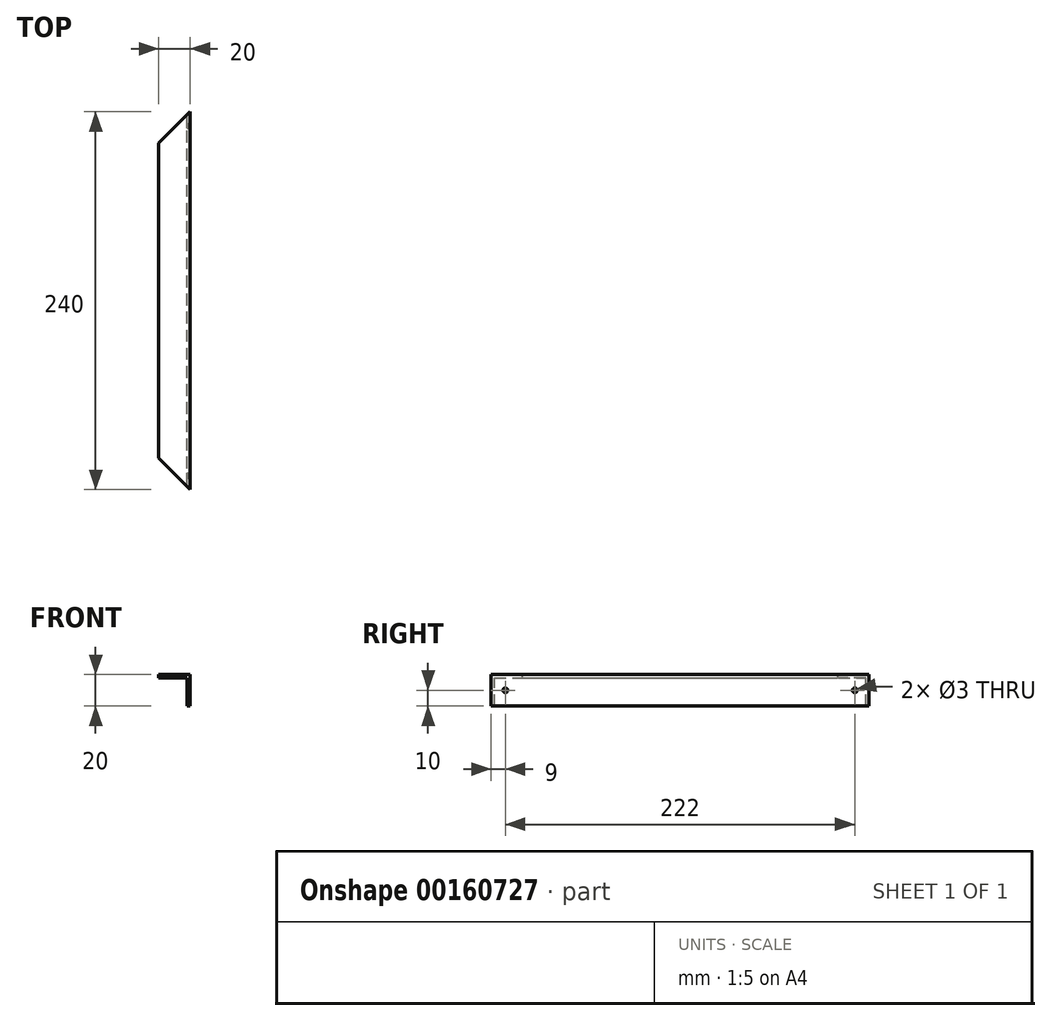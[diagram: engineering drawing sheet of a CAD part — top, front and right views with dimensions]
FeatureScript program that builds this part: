
annotation { "Feature Type Name" : "Feature", "Feature Type Description" : "" }
export const myFeature = defineFeature(function(context is Context, id is Id, definition is map)
    precondition{}
    {
        {
            var Q0;
            Q0=qCreatedBy(makeId("Front.planeOp"),FACE);
            var sketch = newSketch(context, id + "F0", { "sketchPlane" : qUnion([Q0])});
            skLineSegment(sketch, "E0", {"start": v(0, 0) * mm, "end": v(0, 20) * mm});
            skLineSegment(sketch, "E1", {"start": v(0, 20) * mm, "end": v(-20, 20) * mm});
            skLineSegment(sketch, "E2", {"start": v(-20, 20) * mm, "end": v(-20, 18) * mm});
            skLineSegment(sketch, "E3", {"start": v(-20, 18) * mm, "end": v(-2, 18) * mm});
            skLineSegment(sketch, "E4", {"start": v(-2, 18) * mm, "end": v(-2, 0) * mm});
            skLineSegment(sketch, "E5", {"start": v(-2, 0) * mm, "end": v(0, 0) * mm});
            skSolve(sketch);
        }
        {
            var Q0;
            Q0=makeQuery(id+"F0.imprint","IMPRINT",FACE,{"disambiguationData":[TD([[makeQuery(id+"F0.imprint","IMPRINT",EDGE,{"derivedFrom":sQuery(id+"F0.wireOp",EDGE,"E0")}),1.0]])]});
            extrude(context, id + "F1", {"entities" : qUnion([Q0]), "endBound" : BoundingType.SYMMETRIC, "depth" : 240 * mm});
        }
        {
            var Q0;
            Q0=makeQuery(id+"F1.opExtrude","CAP_EDGE",EDGE,{"disambiguationData":[OSD([sQuery(id+"F0.wireOp",EDGE,"E2")])],"isStart":false});
            var Q1;
            Q1=makeQuery(id+"F1.opExtrude","CAP_EDGE",EDGE,{"disambiguationData":[OSD([sQuery(id+"F0.wireOp",EDGE,"E2")])],"isStart":true});
            chamfer(context, id + "F2", {"entities" : qUnion([Q0, Q1]), "width" : 20 * mm, "tangentPropagation" : true});
        }
        {
            var Q0;
            Q0=makeQuery(id+"F1.opExtrude","SWEPT_FACE",FACE,{"disambiguationData":[OSD([sQuery(id+"F0.wireOp",EDGE,"E0")])]});
            var sketch = newSketch(context, id + "F3", { "sketchPlane" : qUnion([Q0])});
            skCircle(sketch, "E6", {"center": v(111, 10) * mm, "radius": 1.5 * mm});
            skCircle(sketch, "E7", {"center": v(-111, 10) * mm, "radius": 1.5 * mm});
            skSolve(sketch);
        }
        {
            var Q0;
            Q0 = qSketchRegion(id + "F3", true);
            extrude(context, id + "F4", {"entities" : qUnion([Q0]), "operationType" : NewBodyOperationType.REMOVE, "endBound" : BoundingType.THROUGH_ALL, "oppositeDirection" : true, "depth" : 25 * mm});
        }
    });
